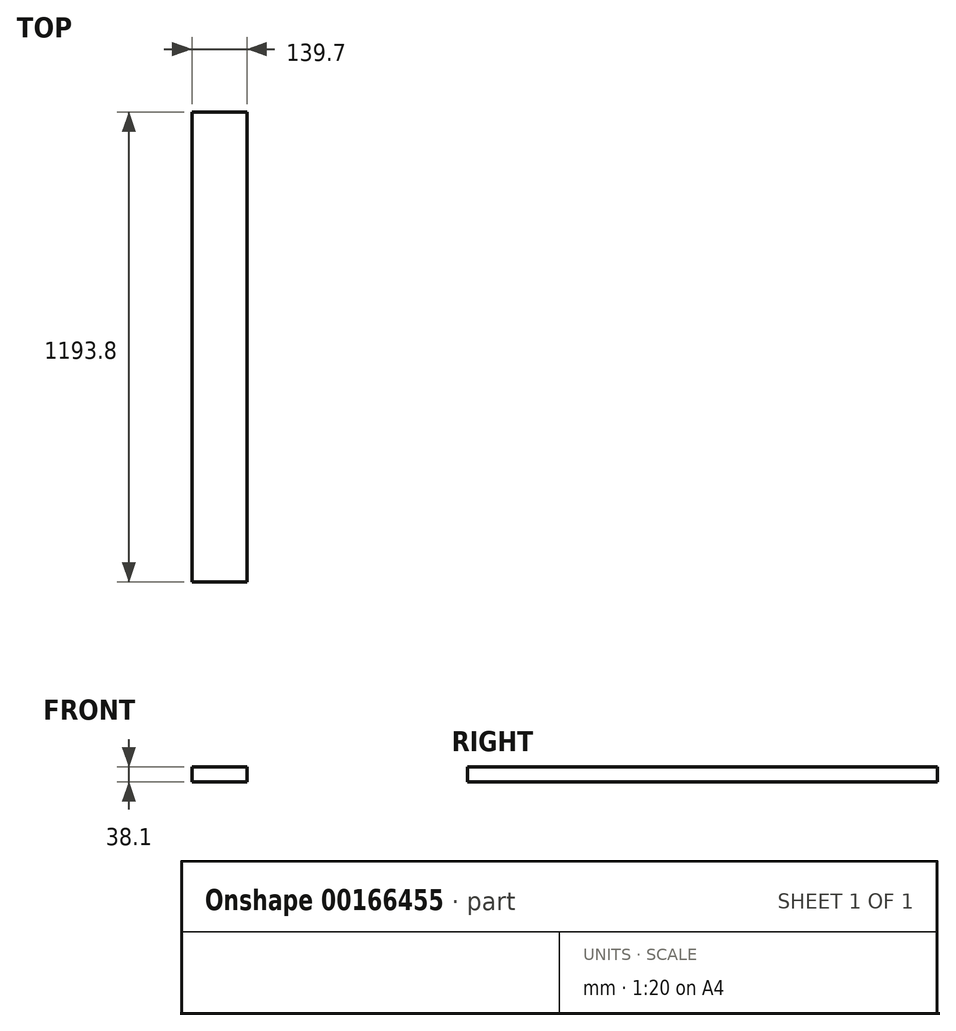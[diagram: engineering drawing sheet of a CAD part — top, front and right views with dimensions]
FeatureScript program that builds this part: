
annotation { "Feature Type Name" : "Feature", "Feature Type Description" : "" }
export const myFeature = defineFeature(function(context is Context, id is Id, definition is map)
    precondition{}
    {
        {
            var Q0;
            Q0=qCreatedBy(makeId("Front.planeOp"),FACE);
            var sketch = newSketch(context, id + "F0", { "sketchPlane" : qUnion([Q0])});
            skLineSegment(sketch, "E0.bottom", {"start": v(-69.85, 19.05) * mm, "end": v(69.85, 19.05) * mm});
            skLineSegment(sketch, "E0.top", {"start": v(-69.85, -19.05) * mm, "end": v(69.85, -19.05) * mm});
            skLineSegment(sketch, "E0.left", {"start": v(-69.85, 19.05) * mm, "end": v(-69.85, -19.05) * mm});
            skLineSegment(sketch, "E0.right", {"start": v(69.85, 19.05) * mm, "end": v(69.85, -19.05) * mm});
            skLineSegment(sketch, "E1", {"start": v(-69.85, 19.05) * mm, "end": v(69.85, -19.05) * mm, "construction": true});
            skSolve(sketch);
        }
        {
            var Q0;
            Q0 = qSketchRegion(id + "F0", true);
            extrude(context, id + "F1", {"entities" : qUnion([Q0]), "endBound" : BoundingType.SYMMETRIC, "depth" : 1193.8 * mm});
        }
    });
